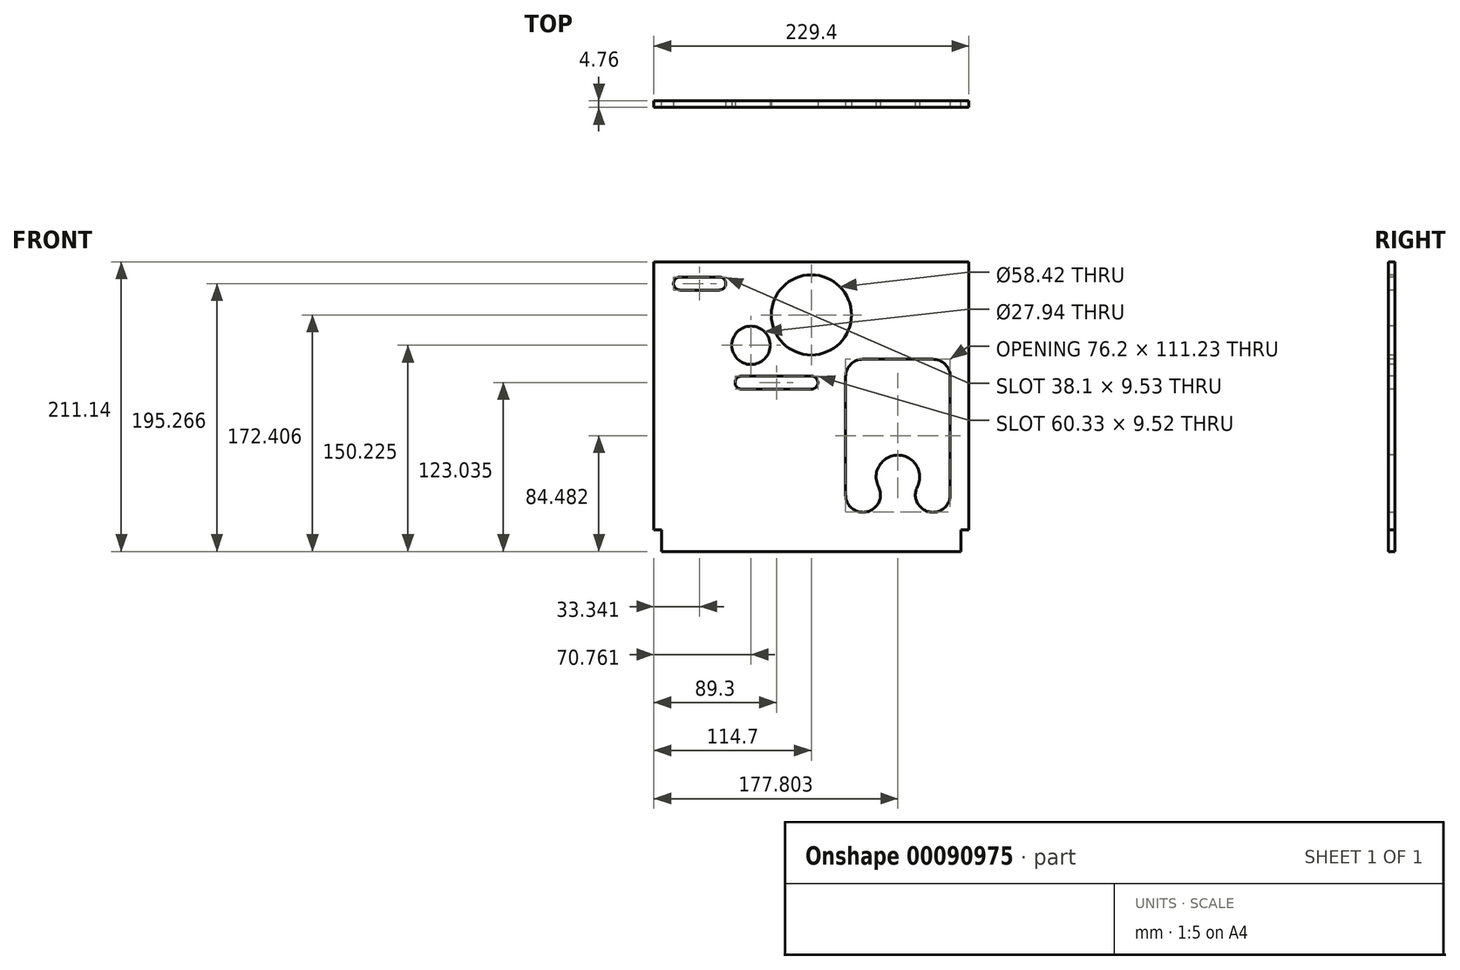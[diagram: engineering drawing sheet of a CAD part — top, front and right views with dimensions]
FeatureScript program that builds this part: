
annotation { "Feature Type Name" : "Feature", "Feature Type Description" : "" }
export const myFeature = defineFeature(function(context is Context, id is Id, definition is map)
    precondition{}
    {
        {
            var Q0;
            Q0=qCreatedBy(makeId("Front.planeOp"),FACE);
            var sketch = newSketch(context, id + "F0", { "sketchPlane" : qUnion([Q0])});
            skLineSegment(sketch, "E0.bottom", {"start": v(114.7, -97.63) * mm, "end": v(-114.7, -97.63) * mm, "construction": true});
            skLineSegment(sketch, "E0.top", {"start": v(114.7, 97.63) * mm, "end": v(-114.7, 97.63) * mm});
            skLineSegment(sketch, "E0.left", {"start": v(114.7, -97.63) * mm, "end": v(114.7, 97.63) * mm});
            skLineSegment(sketch, "E0.right", {"start": v(-114.7, -97.63) * mm, "end": v(-114.7, 97.63) * mm});
            skPoint(sketch, "E0.middle", {"position": v(0, 0) * mm});
            skLineSegment(sketch, "E1", {"start": v(-114.7, -97.63) * mm, "end": v(-109.14, -97.63) * mm});
            skLineSegment(sketch, "E2", {"start": v(-109.14, -97.63) * mm, "end": v(-109.14, -113.5) * mm});
            skLineSegment(sketch, "E3", {"start": v(-109.14, -113.5) * mm, "end": v(109.14, -113.5) * mm});
            skLineSegment(sketch, "E4", {"start": v(109.14, -113.5) * mm, "end": v(109.14, -97.63) * mm});
            skLineSegment(sketch, "E5", {"start": v(109.14, -97.63) * mm, "end": v(114.7, -97.63) * mm});
            skSolve(sketch);
        }
        {
            var Q0;
            Q0=makeQuery(id+"F0.imprint","IMPRINT",FACE,{"disambiguationData":[TD([[makeQuery(id+"F0.imprint","IMPRINT",EDGE,{"derivedFrom":sQuery(id+"F0.wireOp",EDGE,"E0.top")}),1.0]])]});
            extrude(context, id + "F1", {"entities" : qUnion([Q0]), "endBound" : BoundingType.SYMMETRIC, "depth" : 4.76 * mm});
        }
        {
            var Q0;
            Q0=makeQuery(id+"F1.opExtrude","CAP_FACE",FACE,{"disambiguationData":[OSD([sQuery(id+"F0.wireOp",EDGE,"E0.top"),sQuery(id+"F0.wireOp",EDGE,"E0.left"),sQuery(id+"F0.wireOp",EDGE,"E0.right"),sQuery(id+"F0.wireOp",EDGE,"E1"),sQuery(id+"F0.wireOp",EDGE,"E2"),sQuery(id+"F0.wireOp",EDGE,"E3"),sQuery(id+"F0.wireOp",EDGE,"E4"),sQuery(id+"F0.wireOp",EDGE,"E5")])],"isStart":false});
            var sketch = newSketch(context, id + "F2", { "sketchPlane" : qUnion([Q0])});
            skLineSegment(sketch, "E6.bottom", {"start": v(25, 42.07) * mm, "end": v(101.2, 42.07) * mm, "construction": true});
            skLineSegment(sketch, "E6.top", {"start": v(25, -84.93) * mm, "end": v(101.2, -84.93) * mm, "construction": true});
            skLineSegment(sketch, "E6.left", {"start": v(25, 42.07) * mm, "end": v(25, -84.93) * mm, "construction": true});
            skLineSegment(sketch, "E6.right", {"start": v(101.2, 42.07) * mm, "end": v(101.2, -84.93) * mm, "construction": true});
            skLineSegment(sketch, "E7", {"start": v(63.1, -84.93) * mm, "end": v(63.1, 42.07) * mm, "construction": true});
            skArc(sketch, "E8", {"start": v(25, -72.23) * mm, "mid": v(40.7, -84.57) * mm, "end": v(49, -66.41) * mm});
            skArc(sketch, "E9", {"start": v(49, -66.41) * mm, "mid": v(63.1, -43.27) * mm, "end": v(77.21, -66.41) * mm});
            skArc(sketch, "E10", {"start": v(101.2, -72.23) * mm, "mid": v(85.5, -84.57) * mm, "end": v(77.21, -66.41) * mm});
            skCircle(sketch, "E11", {"center": v(63.1, -11.52) * mm, "radius": 31.75 * mm, "construction": true});
            skLineSegment(sketch, "E12", {"start": v(25, 13.88) * mm, "end": v(25, -72.23) * mm});
            skLineSegment(sketch, "E13", {"start": v(101.2, 13.88) * mm, "end": v(101.2, -72.23) * mm});
            skArc(sketch, "E14", {"start": v(25, 13.88) * mm, "mid": v(28.72, 22.86) * mm, "end": v(37.7, 26.58) * mm});
            skArc(sketch, "E15", {"start": v(101.2, 13.88) * mm, "mid": v(97.48, 22.86) * mm, "end": v(88.5, 26.58) * mm});
            skLineSegment(sketch, "E16", {"start": v(37.7, 26.58) * mm, "end": v(88.5, 26.58) * mm});
            skSolve(sketch);
        }
        {
            var Q0;
            Q0 = qSketchRegion(id + "F2", true);
            extrude(context, id + "F3", {"entities" : qUnion([Q0]), "operationType" : NewBodyOperationType.REMOVE, "endBound" : BoundingType.THROUGH_ALL, "oppositeDirection" : true, "depth" : 25.4 * mm});
        }
        {
            var Q0;
            Q0=makeQuery(id+"F1.opExtrude","CAP_FACE",FACE,{"disambiguationData":[OSD([sQuery(id+"F0.wireOp",EDGE,"E0.top"),sQuery(id+"F0.wireOp",EDGE,"E0.left"),sQuery(id+"F0.wireOp",EDGE,"E0.right"),sQuery(id+"F0.wireOp",EDGE,"E1"),sQuery(id+"F0.wireOp",EDGE,"E2"),sQuery(id+"F0.wireOp",EDGE,"E3"),sQuery(id+"F0.wireOp",EDGE,"E4"),sQuery(id+"F0.wireOp",EDGE,"E5")])],"isStart":false});
            var sketch = newSketch(context, id + "F4", { "sketchPlane" : qUnion([Q0])});
            skCircle(sketch, "E17", {"center": v(0, 58.9) * mm, "radius": 29.21 * mm});
            skSolve(sketch);
        }
        {
            var Q0;
            Q0 = qSketchRegion(id + "F4", true);
            extrude(context, id + "F5", {"entities" : qUnion([Q0]), "operationType" : NewBodyOperationType.REMOVE, "endBound" : BoundingType.THROUGH_ALL, "oppositeDirection" : true, "depth" : 25.4 * mm});
        }
        {
            var Q0;
            Q0=makeQuery(id+"F1.opExtrude","CAP_FACE",FACE,{"disambiguationData":[OSD([sQuery(id+"F0.wireOp",EDGE,"E0.top"),sQuery(id+"F0.wireOp",EDGE,"E0.left"),sQuery(id+"F0.wireOp",EDGE,"E0.right"),sQuery(id+"F0.wireOp",EDGE,"E1"),sQuery(id+"F0.wireOp",EDGE,"E2"),sQuery(id+"F0.wireOp",EDGE,"E3"),sQuery(id+"F0.wireOp",EDGE,"E4"),sQuery(id+"F0.wireOp",EDGE,"E5")])],"isStart":false});
            var sketch = newSketch(context, id + "F6", { "sketchPlane" : qUnion([Q0])});
            skLineSegment(sketch, "E18", {"start": v(0, 9.53) * mm, "end": v(-50.8, 9.53) * mm, "construction": true});
            skArc(sketch, "E19", {"start": v(-50.8, 4.76) * mm, "mid": v(-55.56, 9.52) * mm, "end": v(-50.8, 14.29) * mm});
            skArc(sketch, "E20", {"start": v(0, 14.29) * mm, "mid": v(4.76, 9.53) * mm, "end": v(0, 4.76) * mm});
            skLineSegment(sketch, "E21", {"start": v(-50.8, 14.29) * mm, "end": v(0, 14.29) * mm});
            skLineSegment(sketch, "E22", {"start": v(0, 4.76) * mm, "end": v(-50.8, 4.76) * mm});
            skLineSegment(sketch, "E23", {"start": v(-95.65, 81.76) * mm, "end": v(-67.07, 81.76) * mm, "construction": true});
            skLineSegment(sketch, "E24", {"start": v(-95.65, 86.52) * mm, "end": v(-67.07, 86.52) * mm});
            skLineSegment(sketch, "E25", {"start": v(-67.07, 77) * mm, "end": v(-95.65, 77) * mm});
            skArc(sketch, "E26", {"start": v(-95.65, 86.52) * mm, "mid": v(-100.4, 81.76) * mm, "end": v(-95.65, 77) * mm});
            skArc(sketch, "E27", {"start": v(-67.07, 86.52) * mm, "mid": v(-62.3, 81.76) * mm, "end": v(-67.07, 77) * mm});
            skSolve(sketch);
        }
        {
            var Q0;
            Q0 = qSketchRegion(id + "F6", true);
            extrude(context, id + "F7", {"entities" : qUnion([Q0]), "operationType" : NewBodyOperationType.REMOVE, "endBound" : BoundingType.THROUGH_ALL, "oppositeDirection" : true, "depth" : 25.4 * mm});
        }
        {
            var Q0;
            Q0=makeQuery(id+"F1.opExtrude","CAP_FACE",FACE,{"disambiguationData":[OSD([sQuery(id+"F0.wireOp",EDGE,"E0.top"),sQuery(id+"F0.wireOp",EDGE,"E0.left"),sQuery(id+"F0.wireOp",EDGE,"E0.right"),sQuery(id+"F0.wireOp",EDGE,"E1"),sQuery(id+"F0.wireOp",EDGE,"E2"),sQuery(id+"F0.wireOp",EDGE,"E3"),sQuery(id+"F0.wireOp",EDGE,"E4"),sQuery(id+"F0.wireOp",EDGE,"E5")])],"isStart":false});
            var sketch = newSketch(context, id + "F8", { "sketchPlane" : qUnion([Q0])});
            skCircle(sketch, "E28", {"center": v(-43.94, 36.72) * mm, "radius": 13.97 * mm});
            skPoint(sketch, "E29", {"position": v(63.1, -11.52) * mm});
            skSolve(sketch);
        }
        {
            var Q0;
            Q0 = qSketchRegion(id + "F8", true);
            extrude(context, id + "F9", {"entities" : qUnion([Q0]), "operationType" : NewBodyOperationType.REMOVE, "endBound" : BoundingType.THROUGH_ALL, "oppositeDirection" : true, "depth" : 25.4 * mm});
        }
    });
